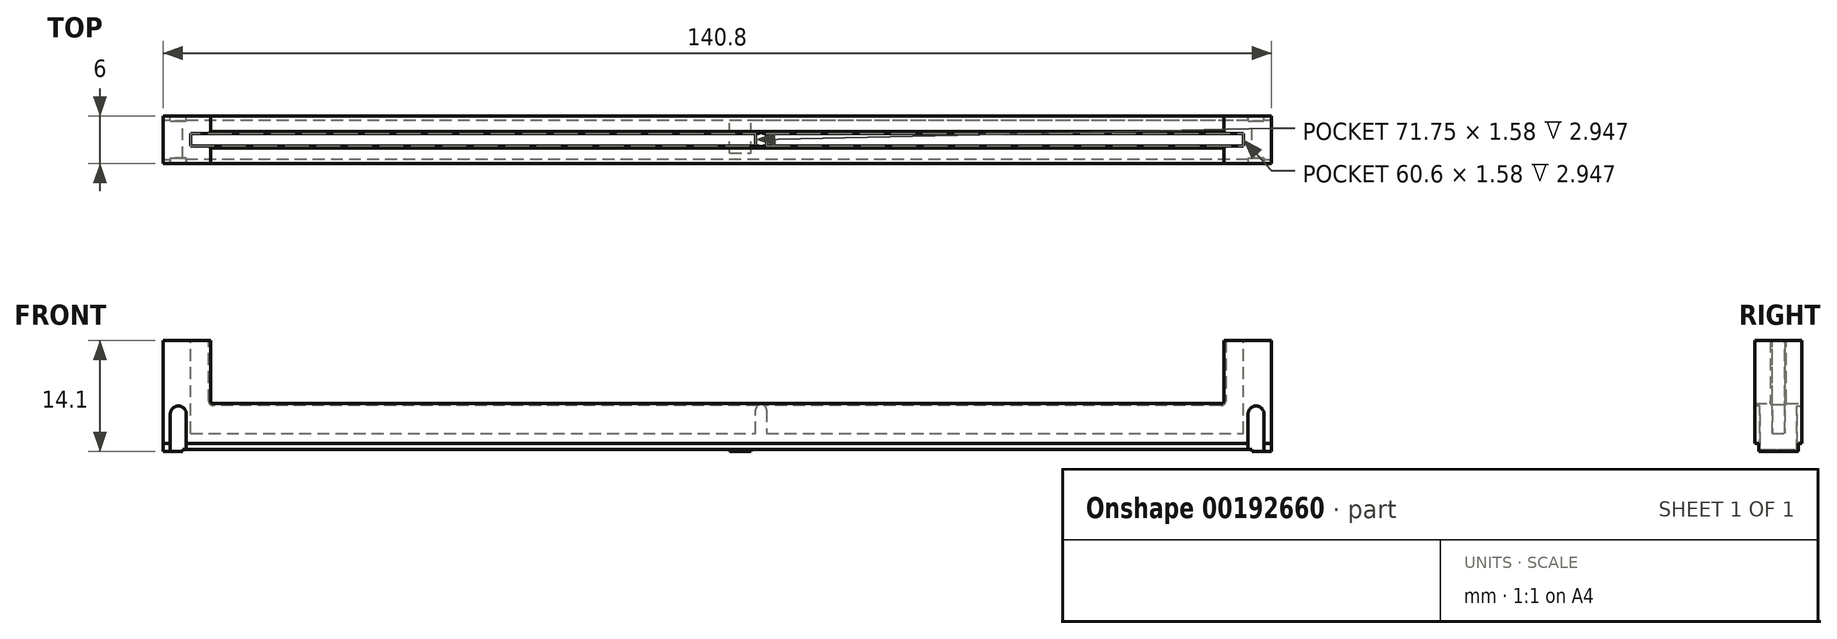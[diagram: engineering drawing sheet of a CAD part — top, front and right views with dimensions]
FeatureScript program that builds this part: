
annotation { "Feature Type Name" : "Feature", "Feature Type Description" : "" }
export const myFeature = defineFeature(function(context is Context, id is Id, definition is map)
    precondition{}
    {
        {
            var Q0;
            Q0=qCreatedBy(makeId("Front.planeOp"),FACE);
            var sketch = newSketch(context, id + "F12", { "sketchPlane" : qUnion([Q0])});
            skLineSegment(sketch, "E0", {"start": v(-67.9, 0.25) * mm, "end": v(1.57, 0.25) * mm});
            skLineSegment(sketch, "E1", {"start": v(67.9, 0.25) * mm, "end": v(67.9, 0) * mm});
            skLineSegment(sketch, "E2", {"start": v(67.9, 0) * mm, "end": v(70.4, 0) * mm});
            skLineSegment(sketch, "E3", {"start": v(70.4, 0) * mm, "end": v(70.4, 14.1) * mm});
            skLineSegment(sketch, "E4", {"start": v(70.4, 14.1) * mm, "end": v(64.35, 14.1) * mm});
            skLineSegment(sketch, "E5", {"start": v(64.35, 14.1) * mm, "end": v(64.35, 6.1) * mm});
            skLineSegment(sketch, "E6", {"start": v(64.35, 6.1) * mm, "end": v(-64.35, 6.1) * mm});
            skLineSegment(sketch, "E7", {"start": v(-64.35, 6.1) * mm, "end": v(-64.35, 14.1) * mm});
            skLineSegment(sketch, "E8", {"start": v(-64.35, 14.1) * mm, "end": v(-70.4, 14.1) * mm});
            skLineSegment(sketch, "E9", {"start": v(-70.4, 14.1) * mm, "end": v(-70.4, 0) * mm});
            skLineSegment(sketch, "E10", {"start": v(-70.4, 0) * mm, "end": v(-67.9, 0) * mm});
            skLineSegment(sketch, "E11", {"start": v(-67.9, 0) * mm, "end": v(-67.9, 0.25) * mm});
            skLineSegment(sketch, "E12", {"start": v(1.57, 0.25) * mm, "end": v(1.57, 0) * mm});
            skLineSegment(sketch, "E13", {"start": v(1.57, 0) * mm, "end": v(4.3, 0) * mm});
            skLineSegment(sketch, "E14", {"start": v(4.3, 0) * mm, "end": v(4.3, 0.25) * mm});
            skLineSegment(sketch, "E15.trimOffspring", {"start": v(4.3, 0.25) * mm, "end": v(67.9, 0.25) * mm});
            skSolve(sketch);
        }
        {
            var Q0;
            Q0 = qSketchRegion(id + "F12", true);
            extrude(context, id + "F13", {"entities" : qUnion([Q0]), "endBound" : BoundingType.SYMMETRIC, "depth" : 6 * mm});
        }
        {
            var Q0;
            Q0=makeQuery(id+"F13.opExtrude","CAP_FACE",FACE,{"disambiguationData":[OSD([sQuery(id+"F12.wireOp",EDGE,"E0"),sQuery(id+"F12.wireOp",EDGE,"E1"),sQuery(id+"F12.wireOp",EDGE,"E2"),sQuery(id+"F12.wireOp",EDGE,"E3"),sQuery(id+"F12.wireOp",EDGE,"E4"),sQuery(id+"F12.wireOp",EDGE,"E5"),sQuery(id+"F12.wireOp",EDGE,"E6"),sQuery(id+"F12.wireOp",EDGE,"E7"),sQuery(id+"F12.wireOp",EDGE,"E8"),sQuery(id+"F12.wireOp",EDGE,"E9"),sQuery(id+"F12.wireOp",EDGE,"E10"),sQuery(id+"F12.wireOp",EDGE,"E11"),sQuery(id+"F12.wireOp",EDGE,"E12"),sQuery(id+"F12.wireOp",EDGE,"E13"),sQuery(id+"F12.wireOp",EDGE,"E14"),sQuery(id+"F12.wireOp",EDGE,"E15.trimOffspring")])],"isStart":false});
            var sketch = newSketch(context, id + "F14", { "sketchPlane" : qUnion([Q0])});
            skLineSegment(sketch, "E16", {"start": v(-69.47, 0) * mm, "end": v(-69.47, 4.75) * mm});
            skLineSegment(sketch, "E17", {"start": v(-67.43, 0.25) * mm, "end": v(-67.43, 4.75) * mm});
            skArc(sketch, "E18", {"start": v(-67.43, 4.75) * mm, "mid": v(-68.45, 5.76) * mm, "end": v(-69.47, 4.75) * mm});
            skLineSegment(sketch, "E19", {"start": v(-69.47, 0) * mm, "end": v(-67.9, 0) * mm});
            skLineSegment(sketch, "E20", {"start": v(-67.9, 0.25) * mm, "end": v(-67.9, 0) * mm});
            skLineSegment(sketch, "E21", {"start": v(-67.43, 0.25) * mm, "end": v(-67.9, 0.25) * mm});
            skLineSegment(sketch, "E22.0", {"start": v(67.9, 0) * mm, "end": v(69.47, 0) * mm});
            skLineSegment(sketch, "E23.0", {"start": v(67.9, 0.25) * mm, "end": v(67.9, 0) * mm});
            skLineSegment(sketch, "E24.0", {"start": v(67.43, 0.25) * mm, "end": v(67.9, 0.25) * mm});
            skLineSegment(sketch, "E25", {"start": v(69.47, 0) * mm, "end": v(69.47, 4.75) * mm});
            skArc(sketch, "E26", {"start": v(69.47, 4.75) * mm, "mid": v(68.45, 5.77) * mm, "end": v(67.43, 4.75) * mm});
            skLineSegment(sketch, "E27", {"start": v(67.43, 4.75) * mm, "end": v(67.43, 0.25) * mm});
            skPoint(sketch, "E28.orphan", {"position": v(4.3, 0.25) * mm});
            skPoint(sketch, "E29.orphan", {"position": v(70.4, 0) * mm});
            skSolve(sketch);
        }
        {
            var Q0;
            Q0 = qSketchRegion(id + "F14", true);
            extrude(context, id + "F0", {"entities" : qUnion([Q0]), "oppositeDirection" : true, "depth" : 0.65 * mm});
        }
        {
            var Q0;
            Q0=makeQuery(id+"F0.opExtrude","SWEPT_BODY",BODY,{"disambiguationData":[OSD([sQuery(id+"F14.wireOp",EDGE,"E16"),sQuery(id+"F14.wireOp",EDGE,"E17"),sQuery(id+"F14.wireOp",EDGE,"E18"),sQuery(id+"F14.wireOp",EDGE,"E19"),sQuery(id+"F14.wireOp",EDGE,"E20"),sQuery(id+"F14.wireOp",EDGE,"E21")])]});
            var Q1;
            Q1=makeQuery(id+"F0.opExtrude","SWEPT_BODY",BODY,{"disambiguationData":[OSD([sQuery(id+"F14.wireOp",EDGE,"E22.0"),sQuery(id+"F14.wireOp",EDGE,"E23.0"),sQuery(id+"F14.wireOp",EDGE,"E24.0"),sQuery(id+"F14.wireOp",EDGE,"E25"),sQuery(id+"F14.wireOp",EDGE,"E26"),sQuery(id+"F14.wireOp",EDGE,"E27")])]});
            var Q2;
            Q2=qCreatedBy(makeId("Front.planeOp"),FACE);
            mirror(context, id + "F15", {"operationType" : NewBodyOperationType.REMOVE, "entities" : qUnion([Q0, Q1]), "mirrorPlane" : qUnion([Q2])});
        }
        {
            var Q0;
            Q0=makeQuery(id+"F0.opExtrude","SWEPT_BODY",BODY,{"disambiguationData":[OSD([sQuery(id+"F14.wireOp",EDGE,"E16"),sQuery(id+"F14.wireOp",EDGE,"E17"),sQuery(id+"F14.wireOp",EDGE,"E18"),sQuery(id+"F14.wireOp",EDGE,"E19"),sQuery(id+"F14.wireOp",EDGE,"E20"),sQuery(id+"F14.wireOp",EDGE,"E21")])]});
            var Q1;
            Q1=makeQuery(id+"F0.opExtrude","SWEPT_BODY",BODY,{"disambiguationData":[OSD([sQuery(id+"F14.wireOp",EDGE,"E22.0"),sQuery(id+"F14.wireOp",EDGE,"E23.0"),sQuery(id+"F14.wireOp",EDGE,"E24.0"),sQuery(id+"F14.wireOp",EDGE,"E25"),sQuery(id+"F14.wireOp",EDGE,"E26"),sQuery(id+"F14.wireOp",EDGE,"E27")])]});
            var Q2;
            Q2=makeQuery(id+"F13.opExtrude","SWEPT_BODY",BODY,{"disambiguationData":[OSD([sQuery(id+"F12.wireOp",EDGE,"E0"),sQuery(id+"F12.wireOp",EDGE,"E1"),sQuery(id+"F12.wireOp",EDGE,"E2"),sQuery(id+"F12.wireOp",EDGE,"E3"),sQuery(id+"F12.wireOp",EDGE,"E4"),sQuery(id+"F12.wireOp",EDGE,"E5"),sQuery(id+"F12.wireOp",EDGE,"E6"),sQuery(id+"F12.wireOp",EDGE,"E7"),sQuery(id+"F12.wireOp",EDGE,"E8"),sQuery(id+"F12.wireOp",EDGE,"E9"),sQuery(id+"F12.wireOp",EDGE,"E10"),sQuery(id+"F12.wireOp",EDGE,"E11"),sQuery(id+"F12.wireOp",EDGE,"E12"),sQuery(id+"F12.wireOp",EDGE,"E13"),sQuery(id+"F12.wireOp",EDGE,"E14"),sQuery(id+"F12.wireOp",EDGE,"E15.trimOffspring")])]});
            booleanBodies(context, id + "F1", {"operationType" : BooleanOperationType.SUBTRACTION, "tools" : qUnion([Q0, Q1]), "targets" : qUnion([Q2])});
        }
        {
            var Q0;
            Q0=makeQuery(id+"F13.opExtrude","CAP_FACE",FACE,{"disambiguationData":[OSD([sQuery(id+"F12.wireOp",EDGE,"E0"),sQuery(id+"F12.wireOp",EDGE,"E1"),sQuery(id+"F12.wireOp",EDGE,"E2"),sQuery(id+"F12.wireOp",EDGE,"E3"),sQuery(id+"F12.wireOp",EDGE,"E4"),sQuery(id+"F12.wireOp",EDGE,"E5"),sQuery(id+"F12.wireOp",EDGE,"E6"),sQuery(id+"F12.wireOp",EDGE,"E7"),sQuery(id+"F12.wireOp",EDGE,"E8"),sQuery(id+"F12.wireOp",EDGE,"E9"),sQuery(id+"F12.wireOp",EDGE,"E10"),sQuery(id+"F12.wireOp",EDGE,"E11"),sQuery(id+"F12.wireOp",EDGE,"E12"),sQuery(id+"F12.wireOp",EDGE,"E13"),sQuery(id+"F12.wireOp",EDGE,"E14"),sQuery(id+"F12.wireOp",EDGE,"E15.trimOffspring")])],"isStart":false});
            var sketch = newSketch(context, id + "F2", { "sketchPlane" : qUnion([Q0])});
            skLineSegment(sketch, "E30.bottom", {"start": v(1.57, 0) * mm, "end": v(4.3, 0) * mm});
            skLineSegment(sketch, "E30.top", {"start": v(1.57, 0.25) * mm, "end": v(4.3, 0.25) * mm});
            skLineSegment(sketch, "E30.left", {"start": v(1.57, 0) * mm, "end": v(1.57, 0.25) * mm});
            skLineSegment(sketch, "E30.right", {"start": v(4.3, 0) * mm, "end": v(4.3, 0.25) * mm});
            skSolve(sketch);
        }
        {
            var Q0;
            Q0 = qSketchRegion(id + "F2", true);
            extrude(context, id + "F3", {"entities" : qUnion([Q0]), "operationType" : NewBodyOperationType.REMOVE, "oppositeDirection" : true, "depth" : 1.3 * mm});
        }
        {
            var Q0;
            Q0=qCreatedBy(makeId("Right.planeOp"),FACE);
            var sketch = newSketch(context, id + "F4", { "sketchPlane" : qUnion([Q0])});
            skLineSegment(sketch, "E31.bottom", {"start": v(-3, 0) * mm, "end": v(-2.5, 0) * mm});
            skLineSegment(sketch, "E31.top", {"start": v(-3, 1) * mm, "end": v(-2.5, 1) * mm});
            skLineSegment(sketch, "E31.left", {"start": v(-3, 0) * mm, "end": v(-3, 1) * mm});
            skLineSegment(sketch, "E31.right", {"start": v(-2.5, 0) * mm, "end": v(-2.5, 1) * mm});
            skLineSegment(sketch, "E32.bottom", {"start": v(2.5, 1) * mm, "end": v(3, 1) * mm});
            skLineSegment(sketch, "E32.top", {"start": v(2.5, 0) * mm, "end": v(3, 0) * mm});
            skLineSegment(sketch, "E32.left", {"start": v(2.5, 1) * mm, "end": v(2.5, 0) * mm});
            skLineSegment(sketch, "E32.right", {"start": v(3, 1) * mm, "end": v(3, 0) * mm});
            skSolve(sketch);
        }
        {
            var Q0;
            Q0 = qSketchRegion(id + "F4", true);
            extrude(context, id + "F5", {"entities" : qUnion([Q0]), "operationType" : NewBodyOperationType.REMOVE, "endBound" : BoundingType.THROUGH_ALL, "oppositeDirection" : true, "depth" : 25 * mm, "hasSecondDirection" : true, "secondDirectionBound" : SecondDirectionBoundingType.THROUGH_ALL, "secondDirectionOppositeDirection" : false, "secondDirectionDepth" : 25 * mm});
        }
        {
            var Q0;
            Q0=makeQuery(id+"F13.opExtrude","SWEPT_FACE",FACE,{"disambiguationData":[OSD([sQuery(id+"F12.wireOp",EDGE,"E8")])]});
            var sketch = newSketch(context, id + "F6", { "sketchPlane" : qUnion([Q0])});
            skLineSegment(sketch, "E33.bottom", {"start": v(-66.88, 0.79) * mm, "end": v(66.88, 0.79) * mm});
            skLineSegment(sketch, "E33.top", {"start": v(-66.88, -0.79) * mm, "end": v(66.88, -0.79) * mm});
            skLineSegment(sketch, "E33.left", {"start": v(-66.88, 0.79) * mm, "end": v(-66.88, -0.79) * mm});
            skLineSegment(sketch, "E33.right", {"start": v(66.88, 0.79) * mm, "end": v(66.88, -0.79) * mm});
            skPoint(sketch, "E33.middle", {"position": v(0, 0) * mm});
            skSolve(sketch);
        }
        {
            var Q0;
            Q0 = qSketchRegion(id + "F6", true);
            extrude(context, id + "F7", {"entities" : qUnion([Q0]), "operationType" : NewBodyOperationType.REMOVE, "oppositeDirection" : true, "depth" : 11.8 * mm});
        }
        {
            var Q0;
            {var subQ0=sQuery(id+"F12.wireOp",EDGE,"E7");var subQ1=sQuery(id+"F12.wireOp",EDGE,"E6");Q0=makeQuery(id+"F7.boolean.opBoolean","SPLIT",EDGE,{"disambiguationData":[TD([makeQuery(id+"F7.opExtrude","SWEPT_FACE",FACE,{"disambiguationData":[OSD([sQuery(id+"F6.wireOp",EDGE,"E33.bottom")])]})])],"derivedFrom":makeQuery(id+"F13.opExtrude","SWEPT_EDGE",EDGE,{"disambiguationData":[OSD([subQ1,subQ0])]})});}
            var Q1;
            {var subQ0=sQuery(id+"F12.wireOp",EDGE,"E7");var subQ1=sQuery(id+"F12.wireOp",EDGE,"E6");Q1=makeQuery(id+"F7.boolean.opBoolean","SPLIT",EDGE,{"disambiguationData":[TD([makeQuery(id+"F7.opExtrude","SWEPT_FACE",FACE,{"disambiguationData":[OSD([sQuery(id+"F6.wireOp",EDGE,"E33.top")])]})])],"derivedFrom":makeQuery(id+"F13.opExtrude","SWEPT_EDGE",EDGE,{"disambiguationData":[OSD([subQ1,subQ0])]})});}
            var Q2;
            {var subQ0=sQuery(id+"F12.wireOp",EDGE,"E6");var subQ1=sQuery(id+"F12.wireOp",EDGE,"E5");Q2=makeQuery(id+"F7.boolean.opBoolean","SPLIT",EDGE,{"disambiguationData":[TD([makeQuery(id+"F7.opExtrude","SWEPT_FACE",FACE,{"disambiguationData":[OSD([sQuery(id+"F6.wireOp",EDGE,"E33.bottom")])]})])],"derivedFrom":makeQuery(id+"F13.opExtrude","SWEPT_EDGE",EDGE,{"disambiguationData":[OSD([subQ1,subQ0])]})});}
            var Q3;
            {var subQ0=sQuery(id+"F12.wireOp",EDGE,"E6");var subQ1=sQuery(id+"F12.wireOp",EDGE,"E5");Q3=makeQuery(id+"F7.boolean.opBoolean","SPLIT",EDGE,{"disambiguationData":[TD([makeQuery(id+"F7.opExtrude","SWEPT_FACE",FACE,{"disambiguationData":[OSD([sQuery(id+"F6.wireOp",EDGE,"E33.top")])]})])],"derivedFrom":makeQuery(id+"F13.opExtrude","SWEPT_EDGE",EDGE,{"disambiguationData":[OSD([subQ1,subQ0])]})});}
            fillet(context, id + "F8", {"entities" : qUnion([Q0, Q1, Q2, Q3]), "radius" : .3 * mm, "tangentPropagation" : true, "allowEdgeOverflow" : false});
        }
        {
            var Q0;
            {var subQ0=sQuery(id+"F6.wireOp",EDGE,"E33.bottom");Q0=makeQuery(id+"F7.boolean.opBoolean","COPY",EDGE,{"disambiguationData":[TD([makeQuery(id+"F13.opExtrude","SWEPT_FACE",FACE,{"disambiguationData":[OSD([sQuery(id+"F12.wireOp",EDGE,"E7")])]})])],"derivedFrom":makeQuery(id+"F7.opExtrude","CAP_EDGE",EDGE,{"disambiguationData":[OSD([subQ0])],"isStart":true})});}
            var Q1;
            Q1=makeQuery(id+"F7.boolean.opBoolean","COPY",EDGE,{"derivedFrom":makeQuery(id+"F7.opExtrude","CAP_EDGE",EDGE,{"disambiguationData":[OSD([sQuery(id+"F6.wireOp",EDGE,"E33.left")])],"isStart":true})});
            var Q2;
            {var subQ0=sQuery(id+"F6.wireOp",EDGE,"E33.top");Q2=makeQuery(id+"F7.boolean.opBoolean","COPY",EDGE,{"disambiguationData":[TD([makeQuery(id+"F13.opExtrude","SWEPT_FACE",FACE,{"disambiguationData":[OSD([sQuery(id+"F12.wireOp",EDGE,"E7")])]})])],"derivedFrom":makeQuery(id+"F7.opExtrude","CAP_EDGE",EDGE,{"disambiguationData":[OSD([subQ0])],"isStart":true})});}
            var Q3;
            Q3=makeQuery(id+"F7.boolean.opBoolean","INTERSECT",EDGE,{"derivedFrom":[makeQuery(id+"F13.opExtrude","SWEPT_FACE",FACE,{"disambiguationData":[OSD([sQuery(id+"F12.wireOp",EDGE,"E7")])]}),makeQuery(id+"F7.opExtrude","SWEPT_FACE",FACE,{"disambiguationData":[OSD([sQuery(id+"F6.wireOp",EDGE,"E33.bottom")])]})]});
            var Q4;
            Q4=makeQuery(id+"F7.boolean.opBoolean","INTERSECT",EDGE,{"derivedFrom":[makeQuery(id+"F13.opExtrude","SWEPT_FACE",FACE,{"disambiguationData":[OSD([sQuery(id+"F12.wireOp",EDGE,"E7")])]}),makeQuery(id+"F7.opExtrude","SWEPT_FACE",FACE,{"disambiguationData":[OSD([sQuery(id+"F6.wireOp",EDGE,"E33.top")])]})]});
            var Q5;
            {var subQ0=sQuery(id+"F6.wireOp",EDGE,"E33.bottom");Q5=makeQuery(id+"F7.boolean.opBoolean","COPY",EDGE,{"disambiguationData":[TD([makeQuery(id+"F13.opExtrude","SWEPT_FACE",FACE,{"disambiguationData":[OSD([sQuery(id+"F12.wireOp",EDGE,"E4")])]})])],"derivedFrom":makeQuery(id+"F7.opExtrude","CAP_EDGE",EDGE,{"disambiguationData":[OSD([subQ0])],"isStart":true})});}
            var Q6;
            Q6=makeQuery(id+"F7.boolean.opBoolean","COPY",EDGE,{"derivedFrom":makeQuery(id+"F7.opExtrude","CAP_EDGE",EDGE,{"disambiguationData":[OSD([sQuery(id+"F6.wireOp",EDGE,"E33.right")])],"isStart":true})});
            var Q7;
            {var subQ0=sQuery(id+"F6.wireOp",EDGE,"E33.top");Q7=makeQuery(id+"F7.boolean.opBoolean","COPY",EDGE,{"disambiguationData":[TD([makeQuery(id+"F13.opExtrude","SWEPT_FACE",FACE,{"disambiguationData":[OSD([sQuery(id+"F12.wireOp",EDGE,"E4")])]})])],"derivedFrom":makeQuery(id+"F7.opExtrude","CAP_EDGE",EDGE,{"disambiguationData":[OSD([subQ0])],"isStart":true})});}
            chamfer(context, id + "F9", {"entities" : qUnion([Q0, Q1, Q2, Q3, Q4, Q5, Q6, Q7]), "width" : .25 * mm, "tangentPropagation" : true});
        }
        {
            var Q0;
            Q0=qCreatedBy(makeId("Front.planeOp"),FACE);
            var sketch = newSketch(context, id + "F10", { "sketchPlane" : qUnion([Q0])});
            skLineSegment(sketch, "E34", {"start": v(5.58, 5.95) * mm, "end": v(5.58, 2.3) * mm, "construction": true});
            skArc(sketch, "E35", {"start": v(6.28, 5.25) * mm, "mid": v(5.58, 5.95) * mm, "end": v(4.88, 5.25) * mm});
            skLineSegment(sketch, "E36", {"start": v(4.87, 5.25) * mm, "end": v(4.87, 2.3) * mm});
            skLineSegment(sketch, "E37", {"start": v(4.87, 2.3) * mm, "end": v(6.28, 2.3) * mm});
            skLineSegment(sketch, "E38", {"start": v(6.28, 2.3) * mm, "end": v(6.28, 5.25) * mm});
            skSolve(sketch);
        }
        {
            var Q0;
            Q0 = qSketchRegion(id + "F10", true);
            extrude(context, id + "F11", {"entities" : qUnion([Q0]), "operationType" : NewBodyOperationType.ADD, "endBound" : BoundingType.SYMMETRIC, "depth" : 2 * mm});
        }
    });
